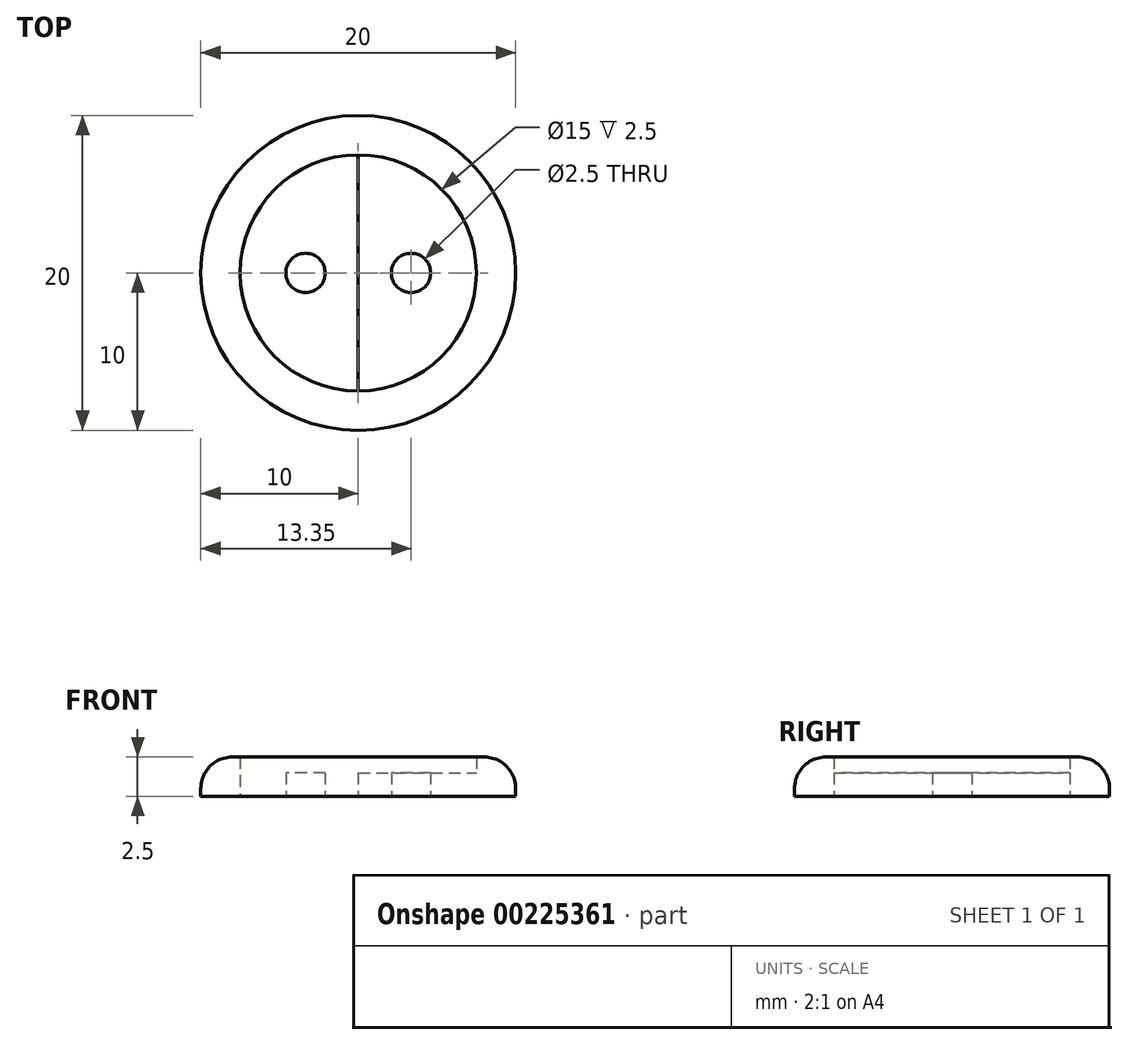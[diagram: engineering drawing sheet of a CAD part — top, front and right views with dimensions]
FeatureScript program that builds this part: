
annotation { "Feature Type Name" : "Feature", "Feature Type Description" : "" }
export const myFeature = defineFeature(function(context is Context, id is Id, definition is map)
    precondition{}
    {
        {
            var Q0;
            Q0=qCreatedBy(makeId("Top.planeOp"),FACE);
            var sketch = newSketch(context, id + "F0", { "sketchPlane" : qUnion([Q0])});
            skCircle(sketch, "E0", {"center": v(0, 0) * mm, "radius": 7.5 * mm});
            skCircle(sketch, "E1", {"center": v(0, 0) * mm, "radius": 10 * mm});
            skLineSegment(sketch, "E2", {"start": v(0, 38.11) * mm, "end": v(0, -48.24) * mm});
            skCircle(sketch, "E3", {"center": v(3.35, 0) * mm, "radius": 1.25 * mm});
            skCircle(sketch, "E4.MirrorC", {"center": v(-3.35, 0) * mm, "radius": 1.25 * mm});
            skSolve(sketch);
        }
        {
            var Q0;
            Q0=qSketchRegion(id+"F0",true);
            extrude(context, id + "F1", {"entities" : qUnion([Q0]), "depth" : 2.5 * mm});
        }
        {
            var Q0;
            Q0=makeQuery(id+"F0.imprint","IMPRINT",FACE,{"disambiguationData":[TD([[makeQuery(id+"F0.imprint","IMPRINT",EDGE,{"derivedFrom":sQuery(id+"F0.wireOp",EDGE,"E4.MirrorC")}),1.0]])]});
            var Q1;
            Q1=makeQuery(id+"F0.imprint","IMPRINT",FACE,{"disambiguationData":[TD([[makeQuery(id+"F0.imprint","IMPRINT",EDGE,{"derivedFrom":sQuery(id+"F0.wireOp",EDGE,"E3")}),-1.0]])]});
            extrude(context, id + "F2", {"entities" : qUnion([Q0, Q1]), "operationType" : NewBodyOperationType.ADD, "depth" : 1.5 * mm});
        }
        {
            var Q0;
            Q0=makeQuery(id+"F1.opExtrude","CAP_EDGE",EDGE,{"disambiguationData":[OSD([sQuery(id+"F0.wireOp",EDGE,"E1")])],"isStart":false});
            fillet(context, id + "F3", {"entities" : qUnion([Q0]), "radius" : 2 * mm, "tangentPropagation" : true, "allowEdgeOverflow" : false});
        }
    });
